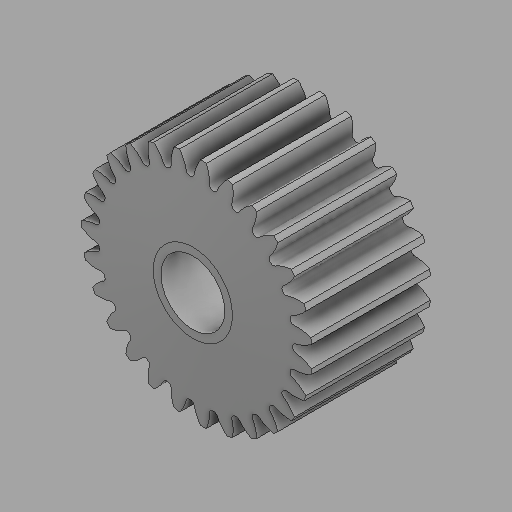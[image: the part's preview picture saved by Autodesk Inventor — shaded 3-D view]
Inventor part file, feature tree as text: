
AUTODESK INVENTOR PART (.ipt)
format: ipt  version: 2024.2 (Build 282272000, 272)  size: 448,512 bytes
history: native  units: in
note: dims shown in document units (in); Inventor stores cm internally (conversion verified against a paired STEP export)
features: mirror x1
ambient origin geometry x8: Origin, YZ Plane, XZ Plane, XY Plane, X Axis, Y Axis, Z Axis, Center Point
bodies: Solid1 (feature_tree)
feature tree (1):
  mirror  "Mirror2"
